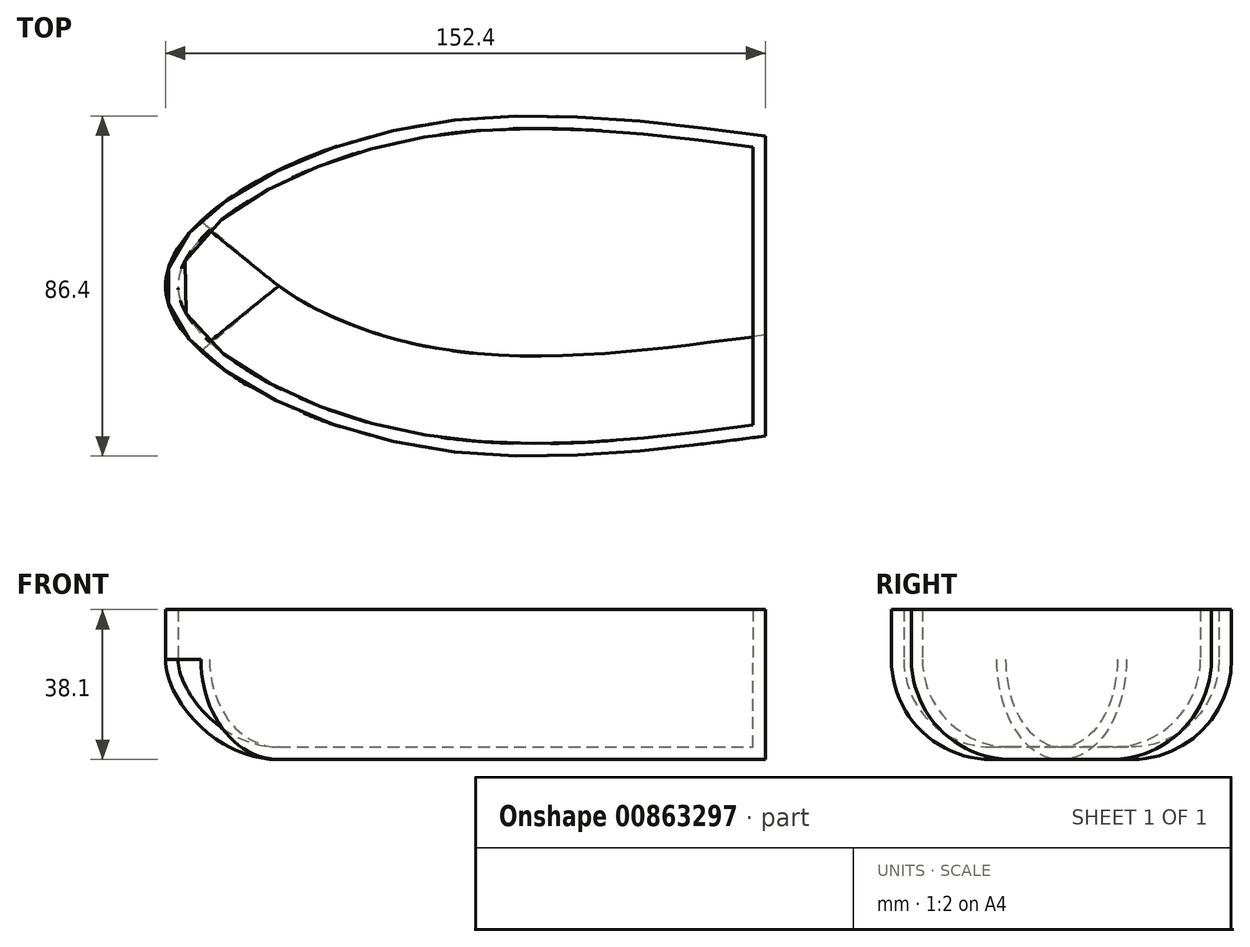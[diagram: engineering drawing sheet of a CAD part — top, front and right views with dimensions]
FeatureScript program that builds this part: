
annotation { "Feature Type Name" : "Feature", "Feature Type Description" : "" }
export const myFeature = defineFeature(function(context is Context, id is Id, definition is map)
    precondition{}
    {
        {
            var Q0;
            Q0=qCreatedBy(makeId("Top.planeOp"),FACE);
            var sketch = newSketch(context, id + "F0", { "sketchPlane" : qUnion([Q0])});
            skLineSegment(sketch, "E0.left", {"start": v(0, 0) * mm, "end": v(0, -76.2) * mm});
            skPoint(sketch, "E1", {"position": v(-152.4, -38.1) * mm});
            skPoint(sketch, "E2", {"position": v(0, -76.2) * mm});
            skPoint(sketch, "E3", {"position": v(0, 0) * mm});
            skFitSpline(sketch, "E4", {"points": [v(0, 0) * mm, v(-100.33, 0) * mm, v(-152.4, -38.1) * mm, v(-100.33, -76.2) * mm, v(0, -76.2) * mm], "startDerivative": vector(-369.7, 48.2) * mm, "endDerivative": vector(369.7, 48.2) * mm});
            skSolve(sketch);
        }
        {
            var Q0;
            Q0=makeQuery(id+"F0.imprint","IMPRINT",FACE,{"disambiguationData":[TD([[makeQuery(id+"F0.imprint","IMPRINT",EDGE,{"derivedFrom":sQuery(id+"F0.wireOp",EDGE,"E0.left")}),-1.0]])]});
            extrude(context, id + "F1", {"entities" : qUnion([Q0]), "depth" : 38.1 * mm, "offsetDistance" : 25.4 * mm});
        }
        {
            var Q0;
            Q0=makeQuery(id+"F1.opExtrude","CAP_EDGE",EDGE,{"disambiguationData":[OSD([sQuery(id+"F0.wireOp",EDGE,"E4")])],"isStart":true});
            fillet(context, id + "F2", {"entities" : qUnion([Q0]), "radius" : 25.4 * mm, "tangentPropagation" : true, "allowEdgeOverflow" : false});
        }
        {
            var Q0;
            Q0=makeQuery(id+"F1.opExtrude","CAP_FACE",FACE,{"disambiguationData":[OSD([sQuery(id+"F0.wireOp",EDGE,"E0.left"),sQuery(id+"F0.wireOp",EDGE,"E4")])],"isStart":false});
            shell(context, id + "F3", {"entities" : qUnion([Q0]), "thickness" : 3.17 * mm});
        }
    });
